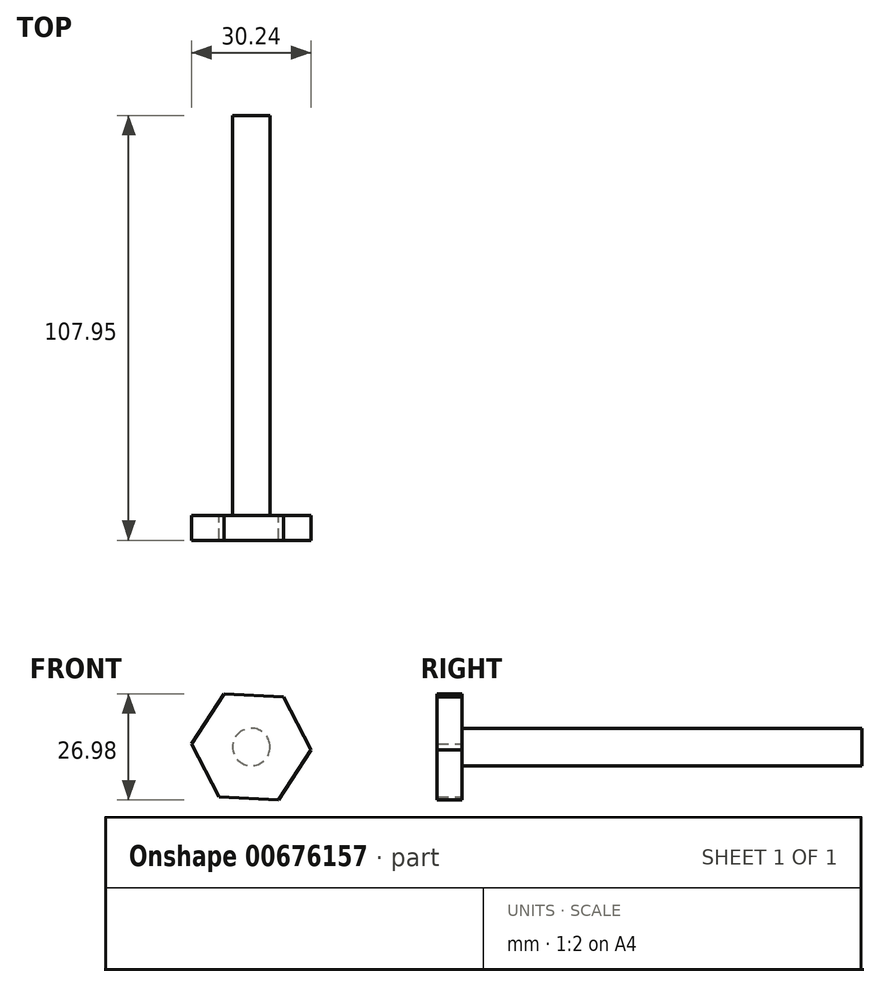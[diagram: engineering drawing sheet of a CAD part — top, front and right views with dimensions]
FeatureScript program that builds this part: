
annotation { "Feature Type Name" : "Feature", "Feature Type Description" : "" }
export const myFeature = defineFeature(function(context is Context, id is Id, definition is map)
    precondition{}
    {
        {
            var Q0;
            Q0=qCreatedBy(makeId("Front.planeOp"),FACE);
            var sketch = newSketch(context, id + "F0", { "sketchPlane" : qUnion([Q0])});
            skCircle(sketch, "E0", {"center": v(0, 0) * mm, "radius": 4.76 * mm});
            skSolve(sketch);
        }
        {
            var Q0;
            Q0 = qSketchRegion(id + "F0", true);
            extrude(context, id + "F1", {"entities" : qUnion([Q0]), "depth" : 101.6 * mm, "offsetDistance" : 25.4 * mm});
        }
        {
            var Q0;
            Q0=makeQuery(id+"F1.opExtrude","CAP_FACE",FACE,{"disambiguationData":[OSD([sQuery(id+"F0.wireOp",EDGE,"E0")])],"isStart":false});
            var sketch = newSketch(context, id + "F2", { "sketchPlane" : qUnion([Q0])});
            skCircle(sketch, "E1.cCircle", {"center": v(0, 0) * mm, "radius": 13.11 * mm, "construction": true});
            skLineSegment(sketch, "E1.0", {"start": v(15.12, -0.79) * mm, "end": v(6.88, -13.49) * mm});
            skLineSegment(sketch, "E1.1", {"start": v(6.88, -13.49) * mm, "end": v(-8.24, -12.7) * mm});
            skLineSegment(sketch, "E1.2", {"start": v(-8.24, -12.7) * mm, "end": v(-15.12, 0.79) * mm});
            skLineSegment(sketch, "E1.3", {"start": v(-15.12, 0.79) * mm, "end": v(-6.88, 13.49) * mm});
            skLineSegment(sketch, "E1.4", {"start": v(-6.88, 13.49) * mm, "end": v(8.24, 12.7) * mm});
            skLineSegment(sketch, "E1.5", {"start": v(8.24, 12.7) * mm, "end": v(15.12, -0.79) * mm});
            skPoint(sketch, "E1.0.midPoint", {"position": v(11, -7.14) * mm});
            skSolve(sketch);
        }
        {
            var Q0;
            Q0 = qSketchRegion(id + "F2", true);
            extrude(context, id + "F3", {"entities" : qUnion([Q0]), "operationType" : NewBodyOperationType.ADD, "depth" : 6.35 * mm, "offsetDistance" : 25.4 * mm});
        }
    });
